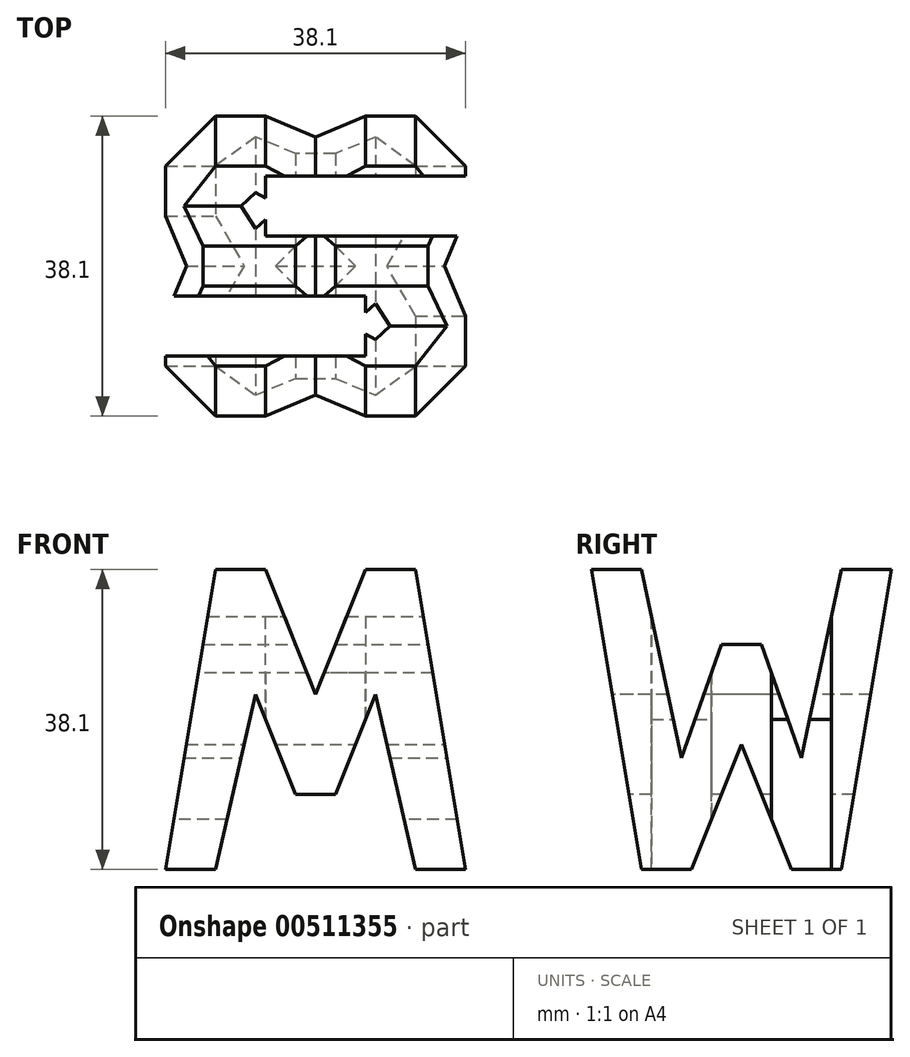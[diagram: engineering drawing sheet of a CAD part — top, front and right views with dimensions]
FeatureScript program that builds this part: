
annotation { "Feature Type Name" : "Feature", "Feature Type Description" : "" }
export const myFeature = defineFeature(function(context is Context, id is Id, definition is map)
    precondition{}
    {
        {
            var Q0;
            Q0=qCreatedBy(makeId("Front.planeOp"),FACE);
            var sketch = newSketch(context, id + "F0", { "sketchPlane" : qUnion([Q0])});
            skLineSegment(sketch, "E0", {"start": v(0, 0) * mm, "end": v(38.1, 0) * mm});
            skLineSegment(sketch, "E1", {"start": v(38.1, 0) * mm, "end": v(38.1, 38.1) * mm});
            skLineSegment(sketch, "E2", {"start": v(38.1, 38.1) * mm, "end": v(0, 38.1) * mm});
            skLineSegment(sketch, "E3", {"start": v(0, 38.1) * mm, "end": v(0, 0) * mm});
            skSolve(sketch);
        }
        {
            var Q0;
            Q0=makeQuery(id+"F0.imprint","IMPRINT",FACE,{"disambiguationData":[TD([[makeQuery(id+"F0.imprint","IMPRINT",EDGE,{"derivedFrom":sQuery(id+"F0.wireOp",EDGE,"E0")}),1.0]])]});
            extrude(context, id + "F1", {"entities" : qUnion([Q0]), "depth" : 38.1 * mm, "offsetDistance" : 25.4 * mm});
        }
        {
            var Q0;
            Q0=qCreatedBy(makeId("Right.planeOp"),FACE);
            cPlane(context, id + "F2", {"entities" : qUnion([Q0]), "cplaneType" : CPlaneType.OFFSET, "offset" : 38.1 * mm, "width" : 152.4 * mm, "height" : 152.4 * mm});
        }
        {
            var Q0;
            Q0=qCreatedBy(makeId("Front.planeOp"),FACE);
            cPlane(context, id + "F3", {"entities" : qUnion([Q0]), "cplaneType" : CPlaneType.OFFSET, "offset" : 38.1 * mm, "width" : 152.4 * mm, "height" : 152.4 * mm});
        }
        {
            var Q0;
            Q0=qCreatedBy(makeId("Top.planeOp"),FACE);
            cPlane(context, id + "F4", {"entities" : qUnion([Q0]), "cplaneType" : CPlaneType.OFFSET, "offset" : 38.1 * mm, "width" : 152.4 * mm, "height" : 152.4 * mm});
        }
        {
            var Q0;
            Q0=qCreatedBy(id+"F2.planeOp",FACE);
            var sketch = newSketch(context, id + "F5", { "sketchPlane" : qUnion([Q0])});
            skLineSegment(sketch, "E4", {"start": v(0, 0) * mm, "end": v(0, 38.1) * mm});
            skLineSegment(sketch, "E5", {"start": v(0, 38.1) * mm, "end": v(-38.1, 38.1) * mm});
            skLineSegment(sketch, "E6", {"start": v(-38.1, 38.1) * mm, "end": v(-38.1, 0) * mm});
            skLineSegment(sketch, "E7", {"start": v(-38.1, 0) * mm, "end": v(0, 0) * mm});
            skLineSegment(sketch, "E8", {"start": v(-38.1, 38.1) * mm, "end": v(-31.75, 0) * mm});
            skLineSegment(sketch, "E9", {"start": v(-25.4, 0) * mm, "end": v(-19.05, 15.88) * mm});
            skPoint(sketch, "E9.endSnap0", {"position": v(-19.05, 0) * mm});
            skLineSegment(sketch, "E10", {"start": v(-19.05, 15.88) * mm, "end": v(-12.7, 0) * mm});
            skLineSegment(sketch, "E11", {"start": v(-6.35, 0) * mm, "end": v(0, 38.1) * mm});
            skLineSegment(sketch, "E12", {"start": v(-31.75, 38.1) * mm, "end": v(-26.67, 14.17) * mm});
            skLineSegment(sketch, "E13", {"start": v(-26.67, 14.17) * mm, "end": v(-21.59, 28.58) * mm});
            skLineSegment(sketch, "E14", {"start": v(-21.59, 28.58) * mm, "end": v(-16.5, 28.58) * mm});
            skLineSegment(sketch, "E15", {"start": v(-16.5, 28.58) * mm, "end": v(-11.43, 14.17) * mm});
            skLineSegment(sketch, "E16", {"start": v(-11.43, 14.17) * mm, "end": v(-6.35, 38.1) * mm});
            skSolve(sketch);
        }
        {
            var Q0;
            {var subQ0=sQuery(id+"F5.wireOp",EDGE,"E12");Q0=makeQuery(id+"F5.imprint","IMPRINT",FACE,{"disambiguationData":[TD([[makeQuery(id+"F5.imprint","IMPRINT",EDGE,{"derivedFrom":subQ0}),1.0]])]});}
            var Q1;
            {var subQ0=sQuery(id+"F5.wireOp",EDGE,"E6");Q1=makeQuery(id+"F5.imprint","IMPRINT",FACE,{"disambiguationData":[TD([[makeQuery(id+"F5.imprint","IMPRINT",EDGE,{"derivedFrom":subQ0}),1.0]])]});}
            var Q2;
            {var subQ0=sQuery(id+"F5.wireOp",EDGE,"E9");Q2=makeQuery(id+"F5.imprint","IMPRINT",FACE,{"disambiguationData":[TD([[makeQuery(id+"F5.imprint","IMPRINT",EDGE,{"derivedFrom":subQ0}),-1.0]])]});}
            var Q3;
            {var subQ0=sQuery(id+"F5.wireOp",EDGE,"E4");Q3=makeQuery(id+"F5.imprint","IMPRINT",FACE,{"disambiguationData":[TD([[makeQuery(id+"F5.imprint","IMPRINT",EDGE,{"derivedFrom":subQ0}),1.0]])]});}
            extrude(context, id + "F6", {"entities" : qUnion([Q0, Q1, Q2, Q3]), "operationType" : NewBodyOperationType.REMOVE, "oppositeDirection" : true, "depth" : 38.1 * mm, "offsetDistance" : 25.4 * mm});
        }
        {
            var Q0;
            Q0=qCreatedBy(id+"F3.planeOp",FACE);
            var sketch = newSketch(context, id + "F7", { "sketchPlane" : qUnion([Q0])});
            skLineSegment(sketch, "E17", {"start": v(0, 0) * mm, "end": v(38.1, 0) * mm});
            skLineSegment(sketch, "E18", {"start": v(38.1, 0) * mm, "end": v(38.1, 38.1) * mm});
            skLineSegment(sketch, "E19", {"start": v(38.1, 38.1) * mm, "end": v(0, 38.1) * mm});
            skLineSegment(sketch, "E20", {"start": v(0, 38.1) * mm, "end": v(0, 0) * mm});
            skLineSegment(sketch, "E21", {"start": v(6.35, 38.1) * mm, "end": v(0, 0) * mm});
            skLineSegment(sketch, "E22", {"start": v(12.7, 38.1) * mm, "end": v(19.05, 22.22) * mm});
            skLineSegment(sketch, "E23", {"start": v(19.05, 22.22) * mm, "end": v(25.4, 38.1) * mm});
            skLineSegment(sketch, "E24", {"start": v(31.75, 38.1) * mm, "end": v(38.1, 0) * mm});
            skLineSegment(sketch, "E25", {"start": v(6.35, 0) * mm, "end": v(11.43, 22.23) * mm});
            skLineSegment(sketch, "E26", {"start": v(11.43, 22.23) * mm, "end": v(16.51, 9.52) * mm});
            skLineSegment(sketch, "E27", {"start": v(16.5, 9.52) * mm, "end": v(21.59, 9.52) * mm});
            skLineSegment(sketch, "E28", {"start": v(21.59, 9.52) * mm, "end": v(26.67, 22.23) * mm});
            skLineSegment(sketch, "E29", {"start": v(26.67, 22.23) * mm, "end": v(31.75, 0) * mm});
            skSolve(sketch);
        }
        {
            var Q0;
            {var subQ0=sQuery(id+"F7.wireOp",EDGE,"E22");Q0=makeQuery(id+"F7.imprint","IMPRINT",FACE,{"disambiguationData":[TD([[makeQuery(id+"F7.imprint","IMPRINT",EDGE,{"derivedFrom":subQ0}),1.0]])]});}
            var Q1;
            {var subQ0=sQuery(id+"F7.wireOp",EDGE,"E20");Q1=makeQuery(id+"F7.imprint","IMPRINT",FACE,{"disambiguationData":[TD([[makeQuery(id+"F7.imprint","IMPRINT",EDGE,{"derivedFrom":subQ0}),1.0]])]});}
            var Q2;
            {var subQ0=sQuery(id+"F7.wireOp",EDGE,"E25");Q2=makeQuery(id+"F7.imprint","IMPRINT",FACE,{"disambiguationData":[TD([[makeQuery(id+"F7.imprint","IMPRINT",EDGE,{"derivedFrom":subQ0}),-1.0]])]});}
            var Q3;
            {var subQ0=sQuery(id+"F7.wireOp",EDGE,"E18");Q3=makeQuery(id+"F7.imprint","IMPRINT",FACE,{"disambiguationData":[TD([[makeQuery(id+"F7.imprint","IMPRINT",EDGE,{"derivedFrom":subQ0}),1.0]])]});}
            extrude(context, id + "F8", {"entities" : qUnion([Q0, Q1, Q2, Q3]), "operationType" : NewBodyOperationType.REMOVE, "oppositeDirection" : true, "depth" : 38.1 * mm, "offsetDistance" : 25.4 * mm});
        }
        {
            var Q0;
            Q0=qCreatedBy(id+"F4.planeOp",FACE);
            var sketch = newSketch(context, id + "F9", { "sketchPlane" : qUnion([Q0])});
            skLineSegment(sketch, "E30", {"start": v(0, 0) * mm, "end": v(38.1, 0) * mm});
            skLineSegment(sketch, "E31", {"start": v(38.1, 0) * mm, "end": v(38.1, -38.1) * mm});
            skLineSegment(sketch, "E32", {"start": v(38.1, -38.1) * mm, "end": v(0, -38.1) * mm});
            skLineSegment(sketch, "E33", {"start": v(0, -38.1) * mm, "end": v(0, 0) * mm});
            skLineSegment(sketch, "E34", {"start": v(38.1, -7.62) * mm, "end": v(12.7, -7.62) * mm});
            skLineSegment(sketch, "E35", {"start": v(12.7, -7.62) * mm, "end": v(12.7, -15.24) * mm});
            skLineSegment(sketch, "E36", {"start": v(12.7, -15.24) * mm, "end": v(38.1, -15.24) * mm});
            skLineSegment(sketch, "E37", {"start": v(0, -22.86) * mm, "end": v(25.4, -22.86) * mm});
            skLineSegment(sketch, "E38", {"start": v(25.4, -22.86) * mm, "end": v(25.4, -30.48) * mm});
            skLineSegment(sketch, "E39", {"start": v(25.4, -30.48) * mm, "end": v(0, -30.48) * mm});
            skSolve(sketch);
        }
        {
            var Q0;
            {var subQ0=sQuery(id+"F9.wireOp",EDGE,"E34");Q0=makeQuery(id+"F9.imprint","IMPRINT",FACE,{"disambiguationData":[TD([[makeQuery(id+"F9.imprint","IMPRINT",EDGE,{"derivedFrom":subQ0}),1.0]])]});}
            var Q1;
            {var subQ0=sQuery(id+"F9.wireOp",EDGE,"E37");Q1=makeQuery(id+"F9.imprint","IMPRINT",FACE,{"disambiguationData":[TD([[makeQuery(id+"F9.imprint","IMPRINT",EDGE,{"derivedFrom":subQ0}),-1.0]])]});}
            extrude(context, id + "F10", {"entities" : qUnion([Q0, Q1]), "operationType" : NewBodyOperationType.REMOVE, "oppositeDirection" : true, "depth" : 38.1 * mm, "offsetDistance" : 25.4 * mm});
        }
    });
